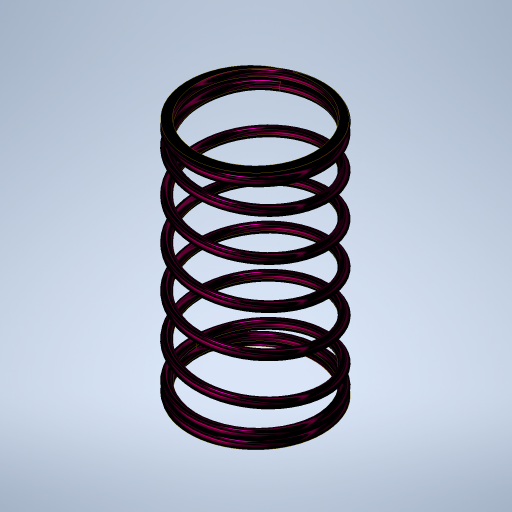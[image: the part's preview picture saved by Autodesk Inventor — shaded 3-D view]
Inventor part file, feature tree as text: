
AUTODESK INVENTOR PART (.ipt)
format: ipt  version: 2023.1 (Build 271208000, 208)  size: 745,984 bytes
history: native  units: in
note: dims shown in document units (in); Inventor stores cm internally (conversion verified against a paired STEP export)
features: sketch x4, helix x3, extrude x2, projected_geometry x1
ambient origin geometry x8: Origin, YZ Plane, XZ Plane, XY Plane, X Axis, Y Axis, Z Axis, Center Point
bodies: Solid1 (feature_tree)
feature tree (10):
  sketch  "Sketch1"  dims[d3=0.55in]
  helix  "Coil1"  [1 undecoded]
  helix  "Coil2"  [1 undecoded]
  extrude  "Extrusion1"  Depth=0.044in
  helix  "Coil3"  [1 undecoded]
  extrude  "Extrusion2"  TaperAngle=0.0deg  [1 undecoded]
  sketch  "Sketch2"  dims[d4=1.0in d5=1.0in d6=1.9685in d7=0.0in d8=30.0deg d9=0.0069in d10=30.0deg d11=0.0069in d12=0.044in]
  sketch  "Sketch3"  dims[d13=1.0in d14=0.7874in d15=0.0in d16=90.0deg d17=90.0deg d18=0.0in d19=0.0in d20=0.0in d21=0.0in]
  sketch  "Sketch4"  dims[d22=0.044in d23=1.0in d24=0.7874in d25=0.0in d26=90.0deg d27=90.0deg d28=0.0in d29=0.0in d30=0.0in d31=0.0in]
  projected_geometry  "Project Cut Edges1"
note: 4 required parameter values undecoded (feature->parameter linkage not recoverable at this tier; creation-order binding heuristic only, values carry confidence <= 0.55)
